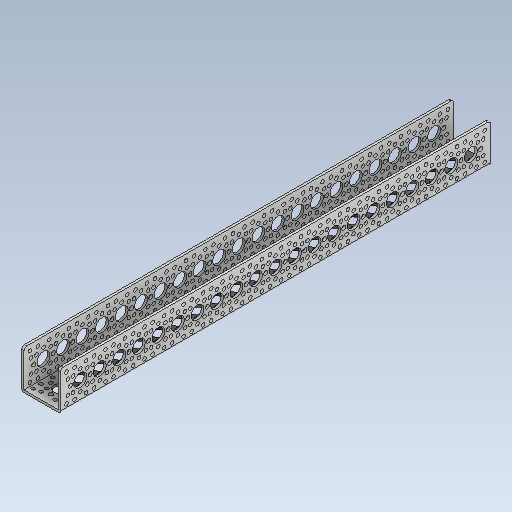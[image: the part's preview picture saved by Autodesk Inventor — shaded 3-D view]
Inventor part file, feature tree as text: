
AUTODESK INVENTOR PART (.ipt)
format: ipt  version: 2020 (Build 240168000, 168)  size: 946,176 bytes
history: native  units: in
note: dims shown in document units (in); Inventor stores cm internally (conversion verified against a paired STEP export)
features: fillet x1
ambient origin geometry x8: Origin, YZ Plane, XZ Plane, XY Plane, X Axis, Y Axis, Z Axis, Center Point
bodies: Solid1 (feature_tree)
feature tree (1):
  fillet  "Fillet1"  [1 undecoded]
note: 1 required parameter value undecoded (feature->parameter linkage not recoverable at this tier; creation-order binding heuristic only, values carry confidence <= 0.55)
